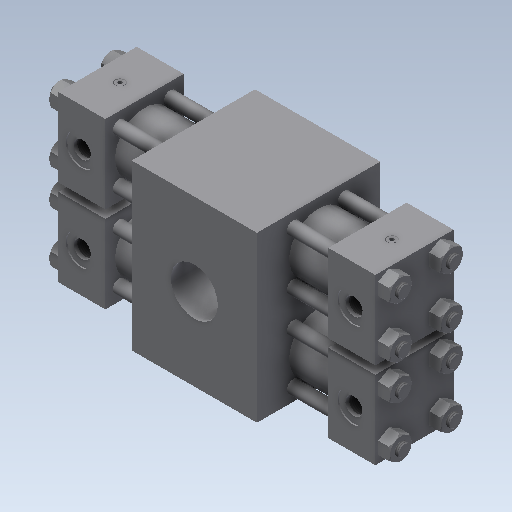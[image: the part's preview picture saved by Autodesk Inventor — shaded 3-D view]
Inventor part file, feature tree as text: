
AUTODESK INVENTOR PART (.ipt)
format: ipt  version: 2021 (Build 250183000, 183)  size: 1,521,664 bytes
history: native  units: in
note: dims shown in document units (in); Inventor stores cm internally (conversion verified against a paired STEP export)
features: other x183, sketch x105, extrude x25, plane x5, chamfer x5, hole x4, mirror x4, pattern_linear x3, projected_geometry x2, fillet x1
ambient origin geometry x8: Origin, YZ Plane, XZ Plane, XY Plane, X Axis, Y Axis, Z Axis, Center Point
bodies: Solid1 (feature_tree), Solid2 (feature_tree), Solid3 (feature_tree)
feature tree (337):
  other  "Table"
  extrude  "Housing"  Depth=4.0in
  other  "Relief_Valve_1"
  other  "Relief_Valve_2"
  extrude  "Relief_Valve_3"  TaperAngle=0.0deg  [1 undecoded]
  other  "Relief_Valve_4"
  extrude  "Relief_Valve_5"  Depth=1.5585in TaperAngle=0.0deg
  extrude  "Cylinder_1"  Depth=2.5in
  plane  "Work Plane1"
  extrude  "Endcap_1"  Depth=2.5in
  extrude  "Pinion_Journal"  Depth=1.5in TaperAngle=0.0deg
  hole  "Face_Mount_1"  [1 undecoded]
  mirror  "Face_Mount_2"
  hole  "Base_Mount"  [1 undecoded]
  other  "P_Mount_1"
  hole  "P_Mount_2"  [1 undecoded]
  fillet  "P_Mount_3"  Radius=0.405in
  other  "Bearing_Cap_1"
  hole  "Bearing_Cap_2"  [1 undecoded]
  other  "WP_CushioningDevice_R"
  other  "Work Axis1"
  extrude  "Tie_Rod_R"  Depth=0.815in
  extrude  "Tie_Rod Extension_R"  Depth=0.5in
  plane  "Work Plane6"
  other  "Tie_Rod Thread_R"
  chamfer  "Tie_Rod Chamfer_R"  Distance=1.0in
  extrude  "Tie_Rod_Nut_R"  TaperAngle=180.0deg  [1 undecoded]
  other  "Tie_Rod_Nut Cut_R"
  pattern_linear  "Tie_Rod Pattern_R"  Spacing1=90.0deg  [1 undecoded]
  plane  "Work Plane20"
  extrude  "Stroke_Adjuster_R_1"  Depth=0.75in
  other  "Stroke_Adjuster_R_2"
  extrude  "Stroke_Adjuster_R_3"  Depth=0.75in
  other  "Stroke_Adjuster_R_4"
  other  "Stroke_Adjuster_R_5"
  extrude  "Stroke_Adjuster_R_6"  Depth=2.5in TaperAngle=45.0deg
  chamfer  "Stroke_Adjuster_R_7"  Distance=0.07in
  mirror  "Mirror1"
  other  "WP_CushioningDevice_L"
  other  "Centre3"
  plane  "Work Plane18"
  extrude  "Stroke_Adjuster_L_1"  TaperAngle=180.0deg  [1 undecoded]
  chamfer  "Stroke_Adjuster_L_2"  Distance=0.0125in Angle=45.0deg
  other  "Stroke_Adjuster_L_3"
  extrude  "Stroke_Adjuster_L_4"  Depth=2.5in
  other  "Stroke_Adjuster_L_5"
  other  "Stroke_Adjuster_L_6"
  extrude  "Stroke_Adjuster_L_7"  Depth=2.5in
  extrude  "Cushioning_Device_R"  Depth=2.5in
  extrude  "Cushioning_Device_L"  Depth=2.5in
  extrude  "Tie_Rod Extension_L"  Depth=2.5in
  other  "Centre2"
  other  "Tie_Rod Thread_L"
  chamfer  "Tie_Rod Chamfer_L"  Distance=0.03in
  extrude  "Tie_Rod_Nut_L"  Depth=2.5in
  other  "Tie_Rod_Nut Cut_L"
  pattern_linear  "Tie_Rod Pattern_L"  Spacing1=90.0deg  [1 undecoded]
  mirror  "Mirror8"
  extrude  "D_Tie_Rod Extension_R"  Depth=2.5in
  extrude  "D_Tie_Rod_Nut_R"  Depth=0.75in
  plane  "Work Plane41"
  other  "D_Tie_Rod_Nut Cut_R"
  other  "D_Tie_Rod Thread_R"
  chamfer  "D_Tie_Rod Chamfer"  Distance=1.3712in
  pattern_linear  "D_Rectangular Pattern"  Spacing1=0.06in  [1 undecoded]
  mirror  "Mirror9"
  other  "Cushion_Plane_1"
  other  "Cushion_R_1"
  other  "Cushion_R_2"
  extrude  "Cushion_R_3"  TaperAngle=45.0deg  [1 undecoded]
  other  "D_Cushion_Plane_1"
  other  "D_Cushion_R_1"
  other  "D_Cushion_R_2"
  extrude  "D_Cushion_R_3"  TaperAngle=90.0deg  [1 undecoded]
  other  "Cushion_Plane_2"
  other  "Cushion_L_1"
  other  "Cushion_L_2"
  extrude  "Cushion_L_3"  Depth=2.5in
  other  "D_Cushion_Plane_2"
  other  "D_Cushion_L_1"
  other  "D_Cushion_L_2"
  extrude  "D_Cushion_L_3"  Depth=2.5in
  other  "Port_Plane_1"
  other  "Port_Sketch_1"
  other  "Port Place Plane_1"
  other  "Port-5_Sketch_1"
  other  "Port_Plane_2"
  other  "Port_Sketch_2"
  other  "Port Place Plane_2"
  other  "Port-5_Sketch_2"
  other  "Con_Port_Sketch_1"
  other  "Con_Port Place Plane_1"
  other  "Con_Port_Sketch_2"
  other  "Con_Port Place Plane_2"
  other  "SAE6_PORT_R"
  other  "SAE6_PORT_L"
  other  "SAE6_PORT-5_R"
  other  "SAE6_PORT-5_L"
  other  "NPTF1/4_PORT_R"
  other  "NPTF1/4_PORT_L"
  other  "NPTF1/4_PORT-5_R"
  other  "NPTF1/4_PORT-5_L"
  other  "BSPP1/4_PORT_R"
  other  "BSPP1/4_PORT_L"
  other  "BSPP1/4_PORT-5_R"
  other  "BSPP1/4_PORT-5_L"
  other  "MetricDINM14_PORT_R"
  other  "MetricDINM14_PORT_L"
  other  "MetricDINM14_PORT-5_R"
  other  "MetricDINM14_PORT-_L"
  other  "MetricISOM14_PORT_R"
  other  "MetricISOM14_PORT_L"
  other  "MetricISOM14_PORT-5_R"
  other  "MetricISOM14_PORT-5_L"
  other  "CON_SAE6_PORT_R"
  other  "CON_SAE6_PORT_L"
  other  "CON_NPTF1/4_PORT_R"
  other  "CON_NPTF1/4_PORT_L"
  other  "CON_BSPP1/4_PORT_R"
  other  "CON_BSPP1/4_PORT_L"
  other  "CON_MetricDINM14_PORT_R"
  other  "CON_MetricDINM14_PORT_L"
  other  "CON_MetricISOM14_PORT_R"
  other  "CON_MetricISOM14_PORT_L"
  other  "D_Port_Plane_1"
  other  "D_Port_Sketch_1"
  other  "D_Port Place Plane_1"
  other  "D_Port-5_Sketch_1"
  other  "D_Port_Plane_2"
  other  "D_Port_Sketch_2"
  other  "D_Port Place Plane_2"
  other  "D_Port-5_Sketch_2"
  other  "D_Con_Port_Sketch_1"
  other  "D_Con_Port Place Plane_1"
  other  "D_Con_Port_Sketch_2"
  other  "D_Con_Port Place Plane_2"
  other  "D_SAE6_PORT_R"
  other  "D_SAE6_PORT_L"
  other  "D_SAE6_PORT-5_R"
  other  "D_SAE6_PORT-5_L"
  other  "D_NPTF1/4_PORT_R"
  other  "D_NPTF1/4_PORT_L"
  other  "D_NPTF1/4_PORT-5_R"
  other  "D_NPTF1/4_PORT-5_L"
  other  "D_BSPP1/4_PORT_R"
  other  "D_BSPP1/4_PORT_L"
  other  "D_BSPP1/4_PORT-5_R"
  other  "D_BSPP1/4_PORT-5_L"
  other  "D_MetricDINM14_PORT_R"
  other  "D_MetricDINM14_PORT_L"
  other  "D_MetricDINM14_PORT-5_R"
  other  "D_MetricDINM14_PORT-5_L"
  other  "D_MetricISOM14_PORT_R"
  other  "D_MetricISOM14_PORT_L"
  other  "D_MetricISOM14_PORT-5_R"
  other  "D_MetricISOM14_PORT-5_L"
  other  "D_CON_SAE6_PORT_R"
  other  "D_CON_SAE6_PORT_L"
  other  "D_CON_NPTF1/4_PORT_R"
  other  "D_CON_NPTF1/4_PORT_L"
  other  "D_CON_BSPP1/4_PORT_R"
  other  "D_CON_BSPP1/4_PORT_L"
  other  "D_CON_MetricDINM14_PORT_R"
  other  "D_CON_MetricDINM14_PORT_L"
  other  "D_CON_MetricISOM14_PORT_R"
  other  "D_CON_MetricISOM14_PORT_L"
  other  "WP_End"
  other  "WP_H"
  other  "WP_Housing-REAR"
  other  "Centre1"
  sketch  "Sketch71"  dims[d125=1.0in d126=0.0in]
  other  "WP_A2"
  other  "WP_A1"
  other  "WP_B1"
  other  "WP_B2"
  other  "WP_C"
  other  "WP_D1"
  other  "WP_D2"
  other  "WP_E1"
  other  "WP_E2"
  other  "WP_F1"
  other  "WP_F2"
  other  "WP_G"
  other  "WP_L2"
  other  "WP_P1"
  other  "WP_P2"
  other  "WP_R1"
  other  "WP_R2"
  other  "WP_S1"
  other  "WP_S2"
  other  "WP_T1"
  other  "Port_1"
  other  "Port_2"
  other  "Port_5_R"
  other  "Port_5_L"
  other  "D_Port_1"
  other  "D_Port_2"
  other  "D_Port_5_R"
  other  "D_Port_5_L"
  other  "WP_Cushion_R"
  other  "WP_Cushion_L"
  other  "D_WP_Cushion_R"
  other  "D_WP_Cushion_L"
  other  "WP_BM1"
  other  "WP_BM2"
  other  "WP_BM3"
  other  "WP_BM4"
  other  "Work Axis20"
  other  "WP_Stroke_R"
  other  "WP_Stroke_L"
  other  "WP_PM1"
  other  "WP_PM2"
  other  "WP_PM3"
  other  "WP_PM4"
  other  "ConPort_1"
  other  "ConPort_2"
  other  "D_ConPort_1"
  other  "D_ConPort_2"
  other  "WP_Pilot1"
  other  "WP_Pilot2"
  other  "WP_Relief_Valve_L"
  other  "WP_Relief_Valve_R"
  sketch  "Sketch3"  dims[d1=4.0in d2=5.25in]
  sketch  "Sketch4"  dims[d3=3.9375in d4=0.0in]
  sketch  "Sketch5"  dims[d5=1.875in d6=1.5in d7=1.38in d8=1.5585in d9=0.0in]
  sketch  "Sketch6"  dims[d10=5.0625in d11=2.5in]
  sketch  "Sketch7"  dims[d12=2.5in d13=1.25in]
  sketch  "Sketch15"  dims[d14=1.38in d15=1.5in d16=0.0in]
  sketch  "Sketch16"  dims[d17=1.5in d18=0.25in d19=0.0in]
  sketch  "Sketch17"  dims[d20=1.5in d21=1.813in]
  other  "Work Axis2"
  sketch  "Sketch18"  dims[d22=0.307in d23=0.5625in d24=0.375in d25=0.25in d26=0.5635in d27=0.6in d28=0.8108in d34=0.8745in d59=0.405in]
  sketch  "Sketch22"  dims[d60=0.815in d61=0.815in]
  sketch  "Sketch27"  dims[d62=0.815in d63=0.815in]
  projected_geometry  "Projected Loop2"
  sketch  "Sketch28"  dims[d64=0.0in d65=0.0in d66=0.5in]
  sketch  "Sketch29"  dims[d67=0.0in d68=1.0in d69=0.0in]
  sketch  "Sketch30"  dims[d71=0.385in d72=0.0in d73=180.0deg]
  sketch  "Sketch31"  dims[d76=45.0deg]
  sketch  "Sketch32"  dims[d78=0.07in]
  sketch  "Sketch35"  dims[d79=45.0deg]
  sketch  "Sketch36"  dims[d83=90.0deg]
  projected_geometry  "Projected Loop3"
  sketch  "Sketch37"  dims[d90=2.5in]
  sketch  "Sketch41"  dims[d97=3.0in]
  sketch  "Sketch42"  dims[d98=3.0in]
  sketch  "Sketch43"  dims[d99=3.0in]
  sketch  "Sketch44"  dims[d100=3.0in]
  sketch  "Sketch49"  dims[d101=0.307in d102=0.5625in d103=0.375in d104=0.25in d105=0.5635in d106=0.6in d107=0.8108in]
  sketch  "Sketch51"  dims[d122=0.0in]
  sketch  "Sketch64"  dims[d123=0.5in]
  sketch  "Sketch66"  dims[d124=0.0in]
  other  "Cushion_Sketch_R"
  other  "Cushion_Sketch_L"
  sketch  "Sketch81"  dims[d128=0.385in d129=0.0in]
  sketch  "Sketch82"  dims[d132=0.07in]
  sketch  "Sketch83"  dims[d133=0.07in]
  sketch  "Sketch85"  dims[d138=90.0deg]
  sketch  "Sketch86"  dims[d145=0.0in]
  sketch  "Sketch87"  dims[d146=0.0in]
  sketch  "Sketch89"  dims[d149=0.0in]
  sketch  "Sketch90"  dims[d150=0.5in]
  sketch  "Sketch91"  dims[d151=1.13in]
  sketch  "Sketch92"  dims[d152=0.0in]
  sketch  "Sketch93"  dims[d153=0.06in d154=0.125in d155=45.0deg]
  sketch  "Sketch94"  dims[d157=0.15in d158=0.0in]
  sketch  "Sketch95"  dims[d164=1.0in d165=0.0in]
  sketch  "Sketch96"  dims[d167=0.323in d168=0.0in]
  sketch  "Sketch97"  dims[d169=0.07in]
  sketch  "Sketch98"  dims[d170=0.07in]
  sketch  "Sketch99"  dims[d171=0.07in]
  other  "Work Axis19"
  sketch  "Sketch100"  dims[d172=0.07in]
  sketch  "Sketch101"  dims[d173=0.323in]
  sketch  "Sketch102"  dims[d174=90.0deg]
  sketch  "Sketch103"  dims[d175=0.0in]
  sketch  "Sketch104"  dims[d176=0.815in]
  sketch  "Sketch105"  dims[d177=0.815in]
  sketch  "Sketch106"  dims[d178=0.405in]
  sketch  "Sketch109"  dims[d179=0.07in]
  sketch  "Sketch111"  dims[d180=0.07in]
  sketch  "Sketch115"  dims[d182=0.385in]
  sketch  "Sketch116"  dims[d183=0.5in]
  sketch  "Sketch117"  dims[d184=1.13in]
  sketch  "Sketch118"  dims[d185=0.0in]
  sketch  "Sketch119"  dims[d198=0.323in d199=0.0in]
  sketch  "Sketch120"  dims[d200=0.07in]
  sketch  "Sketch125"  dims[d201=0.07in]
  sketch  "Sketch126"  dims[d202=0.07in]
  sketch  "Sketch127"  dims[d204=90.0deg]
  sketch  "Sketch128"  dims[d205=1.0in d206=0.0in]
  sketch  "Sketch129"  dims[d208=0.15in d209=0.0in]
  sketch  "Sketch130"  dims[d210=0.0in]
  sketch  "Sketch131"  dims[d211=0.0in]
  sketch  "Sketch132"  dims[d212=2.5in]
  other  "Work Axis21"
  other  "Work Axis22"
  sketch  "Sketch137"  dims[d221=1.219in]
  sketch  "Sketch138"  dims[d225=1.219in]
  sketch  "Sketch139"  dims[d227=-0.72in]
  sketch  "Sketch140"  dims[d228=-0.72in]
  sketch  "Sketch141"  dims[d229=0.0in]
  sketch  "Sketch142"  dims[d230=0.0in d232=0.0in]
  sketch  "Sketch143"  dims[d233=0.0in]
  sketch  "Sketch144"  dims[d234=0.0in]
  sketch  "Sketch145"  dims[d235=0.0in]
  sketch  "Sketch146"  dims[d236=0.0in]
  sketch  "Sketch147"  dims[d272=1.219in]
  sketch  "Sketch148"  dims[d274=0.0in]
  sketch  "Sketch149"  dims[d275=0.0in]
  sketch  "Sketch150"  dims[d276=1.219in]
  sketch  "Sketch151"  dims[d278=0.0in]
  sketch  "Sketch152"  dims[d279=0.0in]
  sketch  "Sketch153"  dims[d290=0.127in]
  sketch  "Sketch154"  dims[d291=1.25in]
  sketch  "Sketch155"  dims[d293=0.06in d294=0.125in d295=45.0deg]
  sketch  "Sketch156"  dims[d300=1.25in]
  sketch  "Sketch157"  dims[d301=90.0deg d302=90.0deg]
  sketch  "Sketch158"  dims[d314=0.123in d316=0.263in d317=0.03in d334=0.108in]
  sketch  "Sketch159"  dims[d338=90.0deg]
  sketch  "Sketch160"  dims[d340=2.5in]
  sketch  "Sketch161"  dims[d341=90.0deg]
  sketch  "Sketch162"  dims[d342=90.0deg]
  sketch  "Sketch163"  dims[d358=90.0deg]
  sketch  "Sketch164"  dims[d360=2.5in]
  sketch  "Sketch165"  dims[d362=90.0deg]
  sketch  "Sketch166"  dims[d363=90.0deg]
  sketch  "Sketch167"  dims[d368=0.123in d369=0.0905in]
  sketch  "Sketch168"  dims[d403=0.078in]
  sketch  "Sketch169"  dims[d406=0.078in]
  sketch  "Sketch170"  dims[d407=90.0deg]
  sketch  "Sketch171"  dims[d409=0.323in]
  sketch  "Sketch172"  dims[d411=0.078in]
  sketch  "Sketch173"  dims[d412=0.078in d415=90.0deg d416=0.75in d418=0.75in d423=0.02in d424=0.125in d425=45.0deg d426=0.07in d440=180.0deg d442=0.0125in d443=0.125in d444=45.0deg d449=0.688in d450=0.688in d452=0.344in d453=0.25in d454=1.3125in d455=0.03in d456=0.03in d457=90.0deg d458=2.25in d459=0.266in d460=0.75in d461=0.375in d462=0.25in d463=0.5635in d464=0.38in d465=0.8108in d466=0.75in d467=1.3712in d469=0.06in d470=45.0deg d471=90.0deg d472=2.25in d473=0.266in d474=0.75in d475=0.375in d476=0.25in d477=0.5635in d478=0.38in d479=0.8108in d480=0.03in d481=0.7874in d483=1.63in d484=0.7874in d486=1.63in d487=0.7874in d489=1.63in d490=0.7874in d492=1.63in d502=0.51in d505=0.06in d506=60.0deg d507=0.15in d508=0.3in d509=0.2529in d510=0.2in d511=0.0454in d512=0.0856in d513=90.0deg d514=0.15in d515=0.0in d516=3.75in d517=3.75in d518=3.75in d519=3.75in d523=0.3753in d530=0.156in d531=30.0deg d532=0.158in d533=0.14in d534=0.311in d545=1.38in d547=0.0156in d548=0.0156in d549=105.0deg d550=0.07in d551=0.14in d552=0.091in d553=0.311in d554=0.123in d555=0.111in d556=2.5in d557=90.0deg d558=90.0deg d559=0.126in d560=0.1in d561=0.0in d562=30.0deg d563=0.311in d564=0.14in d565=0.0312in d567=2.5in d568=90.0deg d578=0.311in d579=0.123in d580=0.07in d581=0.0156in d582=0.0156in d583=0.241in d584=0.14in d585=0.111in d586=0.091in d596=105.0deg d597=90.0deg d598=0.126in d599=0.1in d600=0.0in d601=1.38in d605=0.5in d606=0.4375in d607=0.25in d608=0.156in d609=0.25in d610=1.38in d611=0.4375in d612=0.5in d613=0.25in d614=0.375in d615=0.25in d616=0.344in d617=0.385in d618=-0.72in d619=-0.72in d620=0.5in d621=0.0in d622=0.688in d623=0.385in d624=0.0in d625=1.0in d626=0.0in d627=0.02in d628=0.125in d629=45.0deg d630=90.0deg d631=0.07in d632=0.07in d633=90.0deg d634=0.7874in d636=1.63in d637=0.7874in d639=1.63in d640=-0.72in d641=2.5in d642=90.0deg d651=90.0deg d652=2.5in d653=90.0deg d656=30.0deg d657=0.158in d658=0.14in d659=0.311in d662=0.0156in d663=0.0156in d664=105.0deg d665=0.07in d666=0.14in d667=0.091in d668=0.311in d669=0.123in d670=0.111in d672=90.0deg d674=0.126in d675=0.1in d676=0.0in d677=-0.72in d678=2.5in d679=90.0deg d681=30.0deg d682=0.158in d683=0.14in d684=0.311in d686=90.0deg d687=2.5in d688=90.0deg d690=0.0156in d691=0.0156in d692=105.0deg d693=0.07in d694=0.14in d695=0.091in d696=0.311in d697=0.123in d698=0.111in d700=90.0deg d701=0.126in d702=0.1in d703=0.0in d704=-0.72in d705=2.5in d706=0.0in d707=0.0in d708=-0.72in d709=2.5in d710=0.0in d711=0.0in d712=1.219in d714=0.0in d715=0.0in d718=1.219in d720=1.219in d722=0.0in d723=0.0in d724=1.219in d726=0.0in d727=0.0in d728=3.75in d729=3.75in d730=3.75in d731=0.0in d732=0.0in d733=3.75in d734=0.0in d735=0.0in d736=0.0in d737=0.0in d738=2.5in d739=0.0in d740=0.0in d741=2.5in d742=0.0in d743=0.0in d744=2.5in d745=0.0in d746=0.0in d747=2.5in d748=0.0in d749=0.0in d750=1.219in d752=1.219in d754=3.75in d755=3.75in d756=1.219in d758=1.219in d760=3.75in d761=3.75in d768=3.7402in d769=3.7402in d770=3.7402in d771=3.7402in d772=3.7402in d773=3.7402in d774=1.25in d776=1.25in d778=1.25in d780=1.25in d782=1.25in d784=1.25in d786=3.1496in d787=3.1496in d788=3.1496in d789=3.1496in d790=3.1496in d791=3.1496in d792=3.7402in d793=3.7402in d794=3.7402in d795=3.7402in d796=3.7402in d797=3.7402in d798=1.25in d800=1.25in d802=1.25in d804=1.25in d806=1.25in d808=1.25in d810=3.1496in d811=3.1496in d812=3.1496in d813=3.1496in d814=3.1496in d815=3.1496in d816=90.0deg d817=0.15in d818=0.0in d819=3.625in]
  other  "Work Axis23"
  other  "Work Axis24"
  other  "PORT_SIZE:SAE_06"
note: 12 required parameter values undecoded (feature->parameter linkage not recoverable at this tier; creation-order binding heuristic only, values carry confidence <= 0.55)
